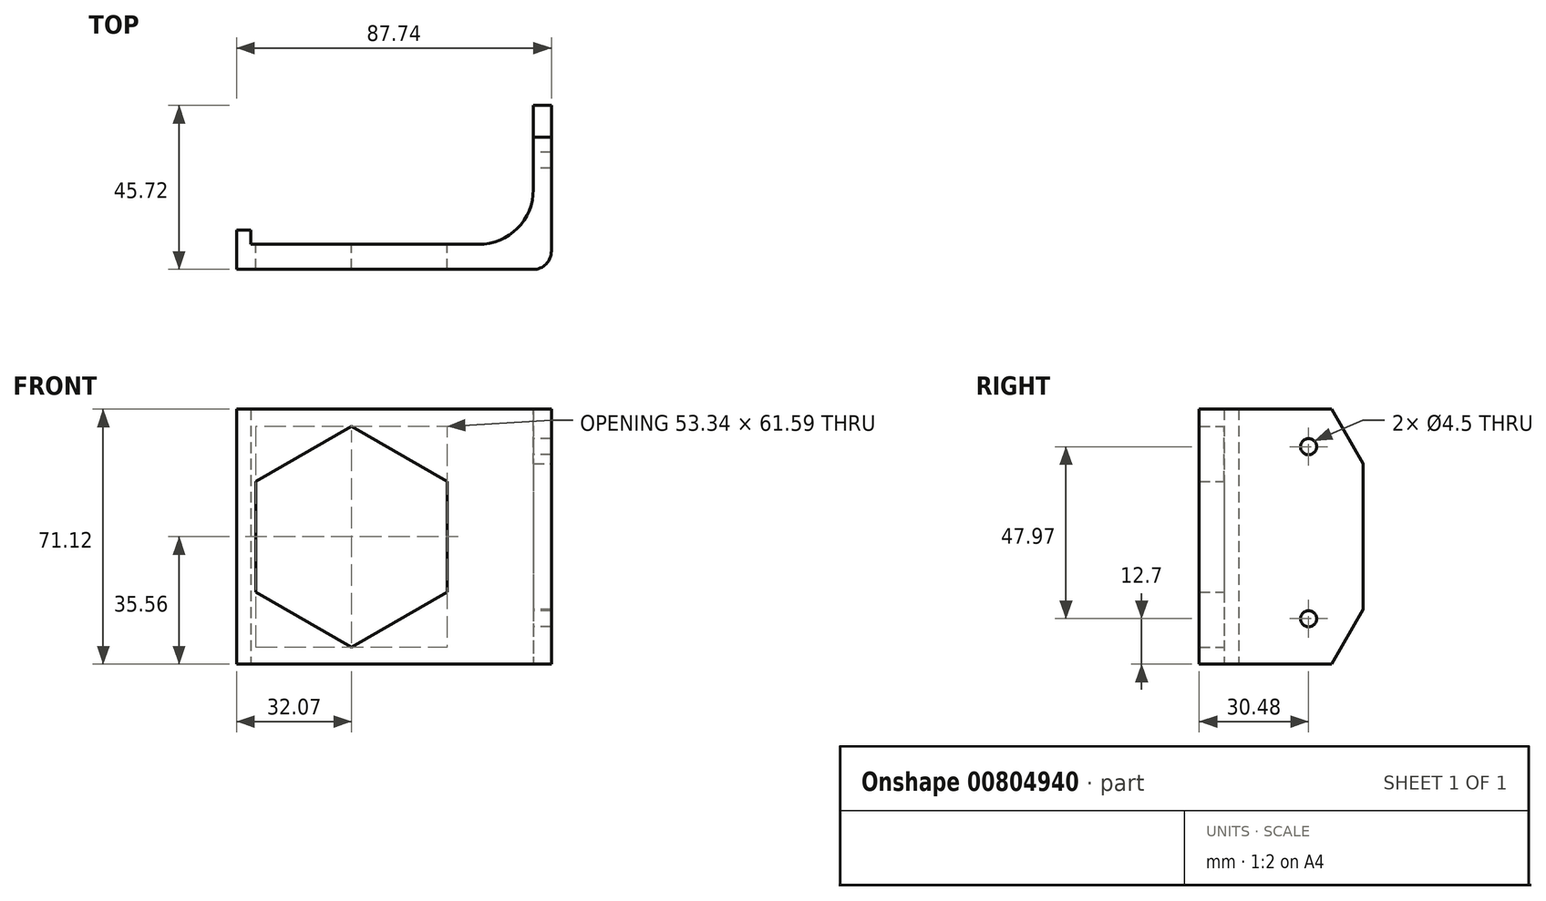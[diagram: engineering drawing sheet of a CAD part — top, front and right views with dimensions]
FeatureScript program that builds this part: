
annotation { "Feature Type Name" : "Feature", "Feature Type Description" : "" }
export const myFeature = defineFeature(function(context is Context, id is Id, definition is map)
    precondition{}
    {
        {
            var Q0;
            Q0=qCreatedBy(makeId("Top.planeOp"),FACE);
            var sketch = newSketch(context, id + "F0", { "sketchPlane" : qUnion([Q0])});
            skLineSegment(sketch, "E0", {"start": v(-78.74, 0) * mm, "end": v(0, 0) * mm});
            skLineSegment(sketch, "E1", {"start": v(0, 0) * mm, "end": v(0, 38.72) * mm});
            skLineSegment(sketch, "E2", {"start": v(0, 38.72) * mm, "end": v(5, 38.72) * mm});
            skLineSegment(sketch, "E3", {"start": v(5, 38.72) * mm, "end": v(5, -7) * mm});
            skLineSegment(sketch, "E4", {"start": v(5, -7) * mm, "end": v(-82.74, -7) * mm});
            skLineSegment(sketch, "E5", {"start": v(-82.74, -7) * mm, "end": v(-82.74, 4) * mm});
            skLineSegment(sketch, "E6", {"start": v(-82.74, 4) * mm, "end": v(-78.74, 4) * mm});
            skLineSegment(sketch, "E7", {"start": v(-78.74, 4) * mm, "end": v(-78.74, 0) * mm});
            skSolve(sketch);
        }
        {
            var Q0;
            Q0 = qSketchRegion(id + "F0", true);
            extrude(context, id + "F1", {"entities" : qUnion([Q0]), "endBound" : BoundingType.SYMMETRIC, "depth" : 71.12 * mm, "offsetDistance" : 25.4 * mm});
        }
        {
            var Q0;
            Q0=makeQuery(id+"F1.opExtrude","SWEPT_FACE",FACE,{"disambiguationData":[OSD([sQuery(id+"F0.wireOp",EDGE,"E0")])]});
            var sketch = newSketch(context, id + "F2", { "sketchPlane" : qUnion([Q0])});
            skCircle(sketch, "E8.cCircle", {"center": v(50.67, 0) * mm, "radius": 26.67 * mm, "construction": true});
            skLineSegment(sketch, "E8.0", {"start": v(50.67, 30.8) * mm, "end": v(77.34, 15.4) * mm});
            skLineSegment(sketch, "E8.1", {"start": v(77.34, 15.4) * mm, "end": v(77.34, -15.4) * mm});
            skLineSegment(sketch, "E8.2", {"start": v(77.34, -15.4) * mm, "end": v(50.67, -30.8) * mm});
            skLineSegment(sketch, "E8.3", {"start": v(50.67, -30.8) * mm, "end": v(24, -15.4) * mm});
            skLineSegment(sketch, "E8.4", {"start": v(24, -15.4) * mm, "end": v(24, 15.4) * mm});
            skLineSegment(sketch, "E8.5", {"start": v(24, 15.4) * mm, "end": v(50.67, 30.8) * mm});
            skPoint(sketch, "E8.0.midPoint", {"position": v(64, 23.1) * mm});
            skSolve(sketch);
        }
        {
            var Q0;
            Q0 = qSketchRegion(id + "F2", true);
            extrude(context, id + "F3", {"entities" : qUnion([Q0]), "operationType" : NewBodyOperationType.REMOVE, "endBound" : BoundingType.THROUGH_ALL, "oppositeDirection" : true, "depth" : 25.4 * mm, "offsetDistance" : 25.4 * mm});
        }
        {
            var Q0;
            Q0=makeQuery(id+"F1.opExtrude","SWEPT_EDGE",EDGE,{"disambiguationData":[OSD([sQuery(id+"F0.wireOp",EDGE,"E0"),sQuery(id+"F0.wireOp",EDGE,"E1")])]});
            fillet(context, id + "F4", {"entities" : qUnion([Q0]), "radius" : 15.24 * mm, "tangentPropagation" : true, "allowEdgeOverflow" : false});
        }
        {
            var Q0;
            Q0=makeQuery(id+"F1.opExtrude","SWEPT_EDGE",EDGE,{"disambiguationData":[OSD([sQuery(id+"F0.wireOp",EDGE,"E3"),sQuery(id+"F0.wireOp",EDGE,"E4")])]});
            fillet(context, id + "F5", {"entities" : qUnion([Q0]), "radius" : 5.08 * mm, "tangentPropagation" : true, "allowEdgeOverflow" : false});
        }
        {
            var Q0;
            Q0=makeQuery(id+"F1.opExtrude","SWEPT_FACE",FACE,{"disambiguationData":[OSD([sQuery(id+"F0.wireOp",EDGE,"E1")])]});
            var sketch = newSketch(context, id + "F6", { "sketchPlane" : qUnion([Q0])});
            skCircle(sketch, "E9", {"center": v(-23.48, 25.1) * mm, "radius": 2.25 * mm});
            skCircle(sketch, "E10", {"center": v(-23.48, -22.86) * mm, "radius": 2.25 * mm});
            skSolve(sketch);
        }
        {
            var Q0;
            Q0 = qSketchRegion(id + "F6", true);
            extrude(context, id + "F7", {"entities" : qUnion([Q0]), "operationType" : NewBodyOperationType.REMOVE, "endBound" : BoundingType.THROUGH_ALL, "oppositeDirection" : true, "depth" : 25.4 * mm, "offsetDistance" : 25.4 * mm});
        }
        {
            var Q0;
            Q0=makeQuery(id+"F1.opExtrude","CAP_EDGE",EDGE,{"disambiguationData":[OSD([sQuery(id+"F0.wireOp",EDGE,"E2")])],"isStart":false});
            var Q1;
            Q1=makeQuery(id+"F1.opExtrude","CAP_EDGE",EDGE,{"disambiguationData":[OSD([sQuery(id+"F0.wireOp",EDGE,"E2")])],"isStart":true});
            chamfer(context, id + "F8", {"entities" : qUnion([Q0, Q1]), "chamferType" : ChamferType.OFFSET_ANGLE, "width" : 15.24 * mm, "oppositeDirection" : false, "angle" : 30 * degree, "tangentPropagation" : true});
        }
    });
